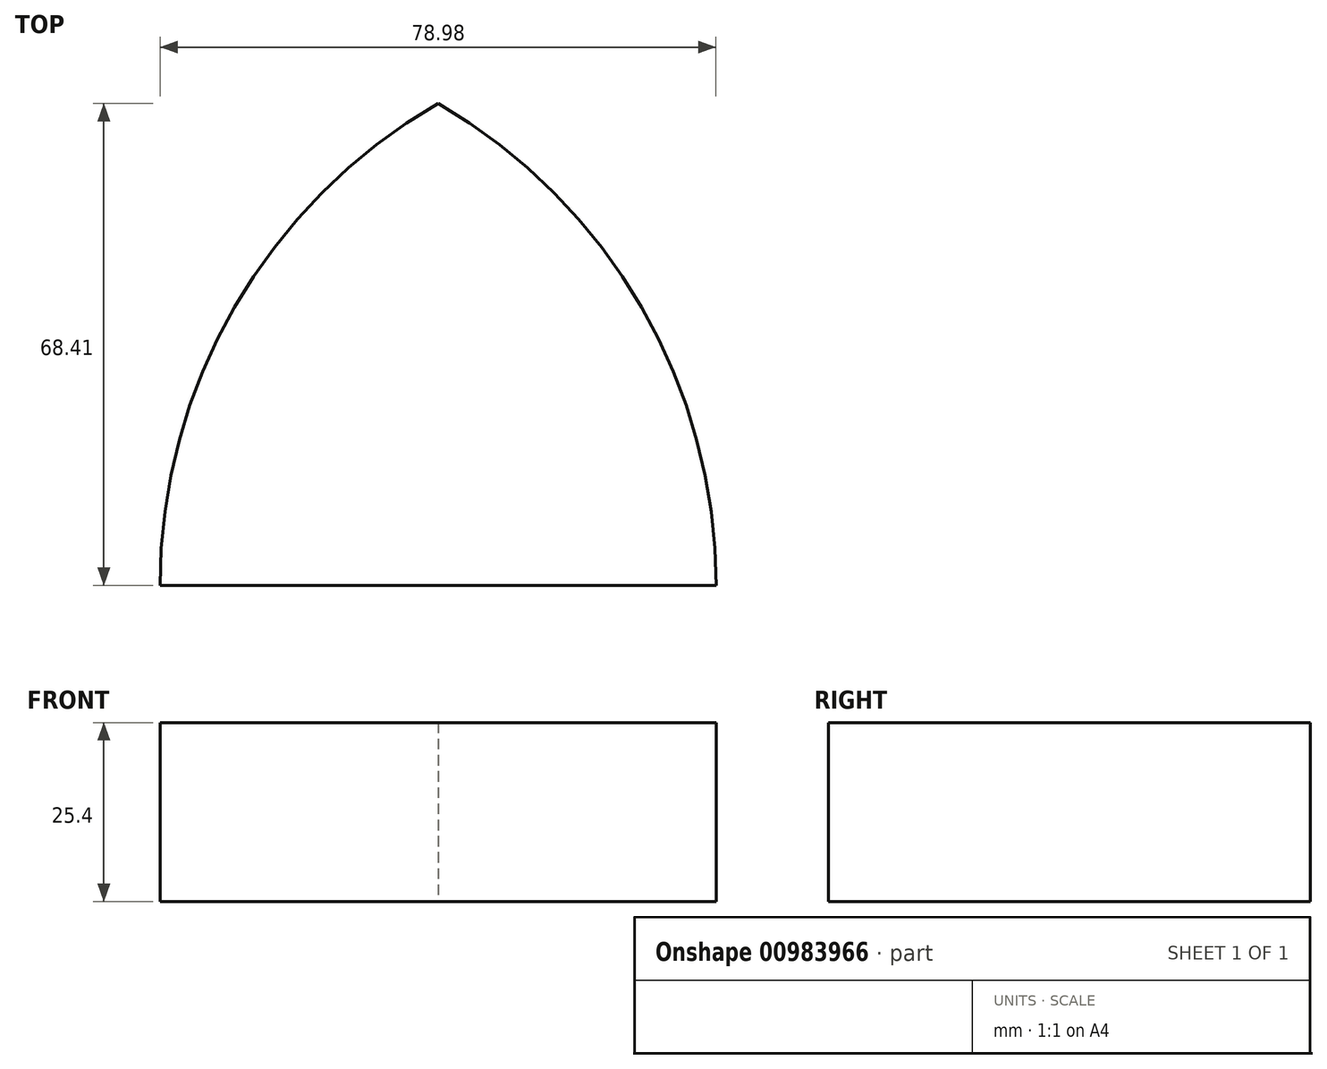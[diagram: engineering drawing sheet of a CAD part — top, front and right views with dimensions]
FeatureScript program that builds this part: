
annotation { "Feature Type Name" : "Feature", "Feature Type Description" : "" }
export const myFeature = defineFeature(function(context is Context, id is Id, definition is map)
    precondition{}
    {
        {
            var Q0;
            Q0=qCreatedBy(makeId("Top.planeOp"),FACE);
            var sketch = newSketch(context, id + "F0", { "sketchPlane" : qUnion([Q0])});
            skArc(sketch, "E0", {"start": v(39.5, 0) * mm, "mid": v(28.91, 39.5) * mm, "end": v(0, 68.4) * mm});
            skLineSegment(sketch, "E1", {"start": v(-39.5, 0) * mm, "end": v(39.5, 0) * mm});
            skArc(sketch, "E2", {"start": v(0, 68.4) * mm, "mid": v(-28.91, 39.5) * mm, "end": v(-39.5, 0) * mm});
            skSolve(sketch);
        }
        {
            var Q0;
            Q0 = qSketchRegion(id + "F0", true);
            extrude(context, id + "F1", {"entities" : qUnion([Q0]), "depth" : 25.4 * mm, "offsetDistance" : 25.4 * mm});
        }
    });
